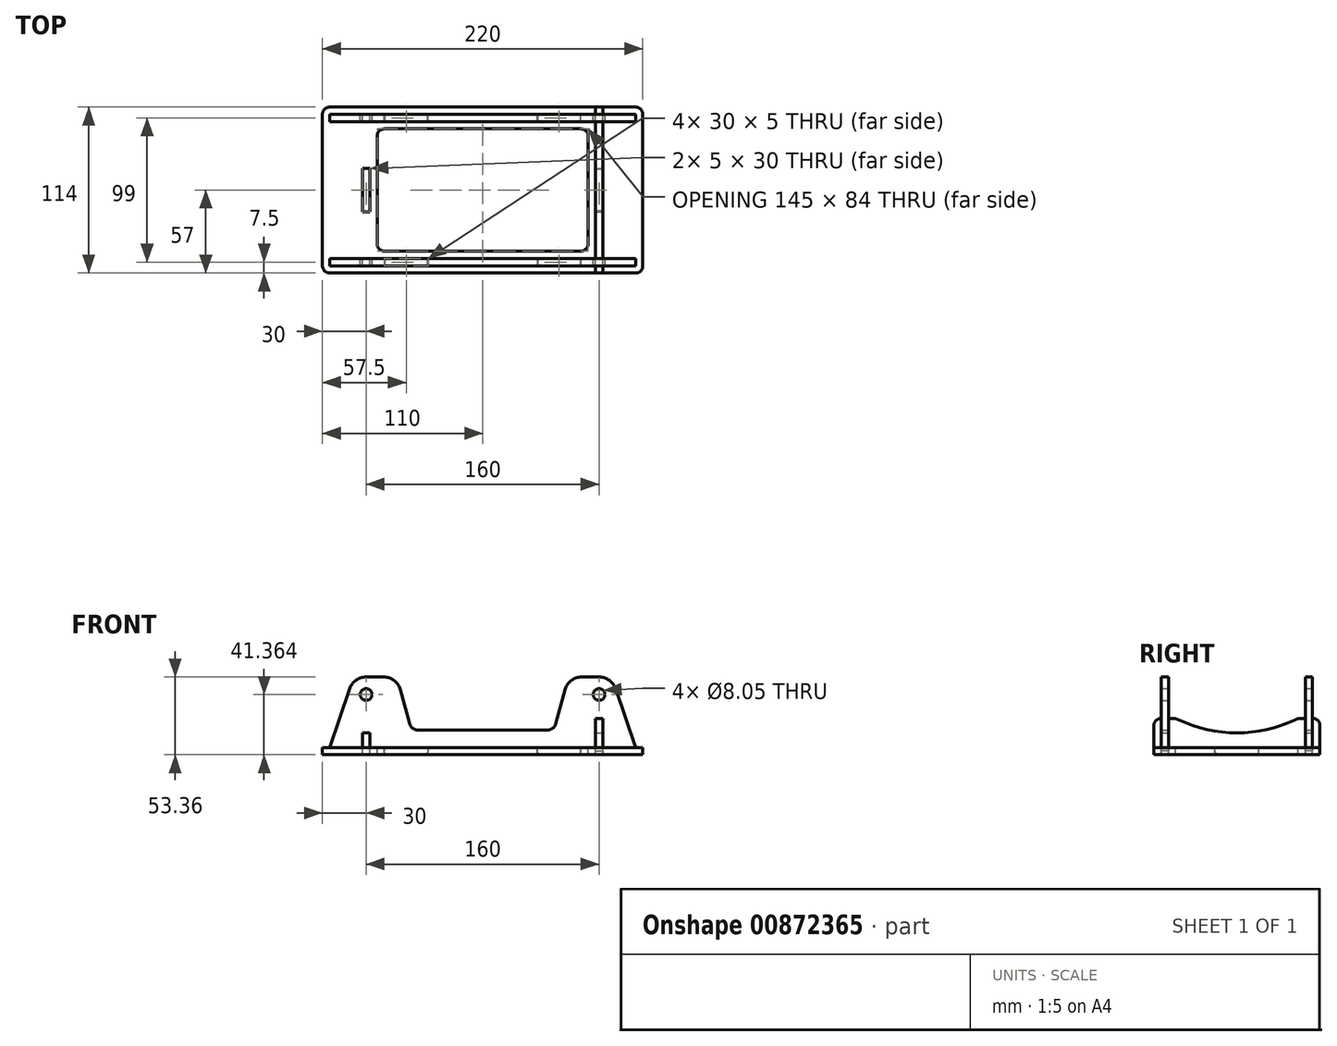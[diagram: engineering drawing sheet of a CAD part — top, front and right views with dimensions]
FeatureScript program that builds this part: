
annotation { "Feature Type Name" : "Feature", "Feature Type Description" : "" }
export const myFeature = defineFeature(function(context is Context, id is Id, definition is map)
    precondition{}
    {
        {
            var Q0;
            Q0=qCreatedBy(makeId("Front.planeOp"),FACE);
            var sketch = newSketch(context, id + "F0", { "sketchPlane" : qUnion([Q0])});
            skCircle(sketch, "E0", {"center": v(0, 135) * mm, "radius": 115 * mm, "construction": true});
            skCircle(sketch, "E1", {"center": v(0, 114.75) * mm, "radius": 100 * mm, "construction": true});
            skCircle(sketch, "E2", {"center": v(-80, 36.36) * mm, "radius": 4.03 * mm});
            skLineSegment(sketch, "E3", {"start": v(-105, 0) * mm, "end": v(-91.36, 40.22) * mm});
            skLineSegment(sketch, "E4", {"start": v(-105, 0) * mm, "end": v(-67.5, 0) * mm});
            skLineSegment(sketch, "E5", {"start": v(-80, 48.36) * mm, "end": v(-68, 48.36) * mm});
            skArc(sketch, "E6", {"start": v(-91.36, 40.22) * mm, "mid": v(-73, 26.61) * mm, "end": v(-80, 48.36) * mm, "construction": true});
            skArc(sketch, "E7", {"start": v(-80, 48.36) * mm, "mid": v(-87, 46.12) * mm, "end": v(-91.36, 40.22) * mm});
            skLineSegment(sketch, "E8.MirrorCS", {"start": v(-50.24, 16.45) * mm, "end": v(-56.4, 39.47) * mm});
            skLineSegment(sketch, "E9", {"start": v(0, 12) * mm, "end": v(-44.44, 12) * mm});
            skPoint(sketch, "E10.visualSharp", {"position": v(-49.05, 12) * mm});
            skArc(sketch, "E10.filletArc", {"start": v(-50.24, 16.45) * mm, "mid": v(-48.1, 13.24) * mm, "end": v(-44.44, 12) * mm});
            skPoint(sketch, "E11.visualSharp", {"position": v(-105, 0) * mm});
            skPoint(sketch, "E12.orphan", {"position": v(0, 0) * mm});
            skArc(sketch, "E13", {"start": v(-68, 48.36) * mm, "mid": v(-75.3, 26.84) * mm, "end": v(-56.4, 39.47) * mm, "construction": true});
            skArc(sketch, "E14", {"start": v(-56.4, 39.47) * mm, "mid": v(-60.7, 45.88) * mm, "end": v(-68, 48.36) * mm});
            skLineSegment(sketch, "E15.MirrorCS", {"start": v(105, 0) * mm, "end": v(67.5, 0) * mm});
            skLineSegment(sketch, "E16.MirrorCS", {"start": v(105, 0) * mm, "end": v(91.36, 40.22) * mm});
            skArc(sketch, "E17.MirrorCS", {"start": v(80, 48.36) * mm, "mid": v(87, 46.12) * mm, "end": v(91.36, 40.22) * mm});
            skCircle(sketch, "E18.MirrorC", {"center": v(80, 36.36) * mm, "radius": 4.03 * mm});
            skLineSegment(sketch, "E19.MirrorCS", {"start": v(80, 48.36) * mm, "end": v(68, 48.36) * mm});
            skArc(sketch, "E20.MirrorCS", {"start": v(56.4, 39.47) * mm, "mid": v(60.7, 45.88) * mm, "end": v(68, 48.36) * mm});
            skLineSegment(sketch, "E21.MirrorCS", {"start": v(50.24, 16.45) * mm, "end": v(56.4, 39.47) * mm});
            skArc(sketch, "E22.MirrorCS", {"start": v(50.24, 16.45) * mm, "mid": v(48.1, 13.24) * mm, "end": v(44.44, 12) * mm});
            skLineSegment(sketch, "E23.MirrorCS", {"start": v(0, 12) * mm, "end": v(44.44, 12) * mm});
            skLineSegment(sketch, "E24.top", {"start": v(-67.5, -5) * mm, "end": v(-37.5, -5) * mm});
            skLineSegment(sketch, "E24.left", {"start": v(-67.5, 0) * mm, "end": v(-67.5, -5) * mm});
            skLineSegment(sketch, "E24.right", {"start": v(-37.5, 0) * mm, "end": v(-37.5, -5) * mm});
            skLineSegment(sketch, "E25", {"start": v(-37.5, 0) * mm, "end": v(0, 0) * mm});
            skLineSegment(sketch, "E26.MirrorCS", {"start": v(67.5, 0) * mm, "end": v(67.5, -5) * mm});
            skLineSegment(sketch, "E27.MirrorCS", {"start": v(67.5, -5) * mm, "end": v(37.5, -5) * mm});
            skLineSegment(sketch, "E28.MirrorCS", {"start": v(37.5, 0) * mm, "end": v(37.5, -5) * mm});
            skLineSegment(sketch, "E29", {"start": v(37.5, 0) * mm, "end": v(0, 0) * mm});
            skLineSegment(sketch, "E30", {"start": v(37.5, 0) * mm, "end": v(37.5, 0) * mm});
            skLineSegment(sketch, "E31.bottom", {"start": v(-77.5, 10) * mm, "end": v(-82.5, 10) * mm});
            skLineSegment(sketch, "E31.top", {"start": v(-77.5, 0) * mm, "end": v(-82.5, 0) * mm});
            skLineSegment(sketch, "E31.left", {"start": v(-77.5, 10) * mm, "end": v(-77.5, 0) * mm});
            skLineSegment(sketch, "E31.right", {"start": v(-82.5, 10) * mm, "end": v(-82.5, 0) * mm});
            skPoint(sketch, "E31.middle", {"position": v(-80, 5) * mm});
            skLineSegment(sketch, "E32.MirrorCS", {"start": v(77.5, 10) * mm, "end": v(82.5, 10) * mm});
            skLineSegment(sketch, "E33.MirrorCS", {"start": v(82.5, 10) * mm, "end": v(82.5, 0) * mm});
            skLineSegment(sketch, "E34.MirrorCS", {"start": v(77.5, 0) * mm, "end": v(82.5, 0) * mm});
            skLineSegment(sketch, "E35.MirrorCS", {"start": v(77.5, 10) * mm, "end": v(77.5, 0) * mm});
            skSolve(sketch);
        }
        {
            var Q0;
            Q0=makeQuery(id+"F0.imprint","IMPRINT",FACE,{"disambiguationData":[TD([[makeQuery(id+"F0.imprint","IMPRINT",EDGE,{"derivedFrom":sQuery(id+"F0.wireOp",EDGE,"E2")}),-1.0]])]});
            extrude(context, id + "F1", {"entities" : qUnion([Q0]), "depth" : 5 * mm, "offsetDistance" : 25 * mm});
        }
        {
            var Q0;
            Q0=makeQuery(id+"F1.opExtrude","SWEPT_EDGE",EDGE,{"disambiguationData":[OSD([sQuery(id+"F0.wireOp",EDGE,"E24.top"),sQuery(id+"F0.wireOp",EDGE,"E24.left")])]});
            var Q1;
            Q1=makeQuery(id+"F1.opExtrude","SWEPT_EDGE",EDGE,{"disambiguationData":[OSD([sQuery(id+"F0.wireOp",EDGE,"E27.MirrorCS"),sQuery(id+"F0.wireOp",EDGE,"E28.MirrorCS")])]});
            var Q2;
            Q2=makeQuery(id+"F1.opExtrude","SWEPT_EDGE",EDGE,{"disambiguationData":[OSD([sQuery(id+"F0.wireOp",EDGE,"E24.top"),sQuery(id+"F0.wireOp",EDGE,"E24.right")])]});
            chamfer(context, id + "F2", {"entities" : qUnion([Q0, Q1, Q2]), "chamferType" : ChamferType.TWO_OFFSETS, "width1" : .5 * mm, "oppositeDirection" : false, "width2" : 2.5 * mm, "tangentPropagation" : true});
        }
        {
            var Q0;
            Q0=makeQuery(id+"F1.opExtrude","SWEPT_EDGE",EDGE,{"disambiguationData":[OSD([sQuery(id+"F0.wireOp",EDGE,"E26.MirrorCS"),sQuery(id+"F0.wireOp",EDGE,"E27.MirrorCS")])]});
            chamfer(context, id + "F3", {"entities" : qUnion([Q0]), "chamferType" : ChamferType.TWO_OFFSETS, "width1" : 2.5 * mm, "oppositeDirection" : false, "width2" : .5 * mm, "tangentPropagation" : true});
        }
        {
            var Q0;
            Q0=makeQuery(id+"F1.opExtrude","SWEPT_BODY",BODY,{"disambiguationData":[OSD([sQuery(id+"F0.wireOp",EDGE,"E2"),sQuery(id+"F0.wireOp",EDGE,"E3"),sQuery(id+"F0.wireOp",EDGE,"E4"),sQuery(id+"F0.wireOp",EDGE,"E5"),sQuery(id+"F0.wireOp",EDGE,"E7"),sQuery(id+"F0.wireOp",EDGE,"E8.MirrorCS"),sQuery(id+"F0.wireOp",EDGE,"E9"),sQuery(id+"F0.wireOp",EDGE,"E10.filletArc"),sQuery(id+"F0.wireOp",EDGE,"E14"),sQuery(id+"F0.wireOp",EDGE,"E15.MirrorCS"),sQuery(id+"F0.wireOp",EDGE,"E16.MirrorCS"),sQuery(id+"F0.wireOp",EDGE,"E17.MirrorCS"),sQuery(id+"F0.wireOp",EDGE,"E18.MirrorC"),sQuery(id+"F0.wireOp",EDGE,"E19.MirrorCS"),sQuery(id+"F0.wireOp",EDGE,"E20.MirrorCS"),sQuery(id+"F0.wireOp",EDGE,"E21.MirrorCS"),sQuery(id+"F0.wireOp",EDGE,"E22.MirrorCS"),sQuery(id+"F0.wireOp",EDGE,"E23.MirrorCS"),sQuery(id+"F0.wireOp",EDGE,"E24.top"),sQuery(id+"F0.wireOp",EDGE,"E24.left"),sQuery(id+"F0.wireOp",EDGE,"E24.right"),sQuery(id+"F0.wireOp",EDGE,"E25"),sQuery(id+"F0.wireOp",EDGE,"E26.MirrorCS"),sQuery(id+"F0.wireOp",EDGE,"E27.MirrorCS"),sQuery(id+"F0.wireOp",EDGE,"E28.MirrorCS"),sQuery(id+"F0.wireOp",EDGE,"E29"),sQuery(id+"F0.wireOp",EDGE,"E31.bottom"),sQuery(id+"F0.wireOp",EDGE,"E31.top"),sQuery(id+"F0.wireOp",EDGE,"E31.left"),sQuery(id+"F0.wireOp",EDGE,"E31.right"),sQuery(id+"F0.wireOp",EDGE,"E32.MirrorCS"),sQuery(id+"F0.wireOp",EDGE,"E33.MirrorCS"),sQuery(id+"F0.wireOp",EDGE,"E34.MirrorCS"),sQuery(id+"F0.wireOp",EDGE,"E35.MirrorCS")])]});
            transform(context, id + "F4", {"entities" : qUnion([Q0]), "transformType" : TransformType.TRANSLATION_3D, "dx" : 0 * mm, "dy" : (94 + 5) * mm, "dz" : 0 * mm, "makeCopy" : true});
        }
        {
            var Q0;
            Q0=makeQuery(id+"F4.opPattern","COPY",FACE,{"derivedFrom":makeQuery(id+"F1.opExtrude","SWEPT_FACE",FACE,{"disambiguationData":[OSD([sQuery(id+"F0.wireOp",EDGE,"E25"),sQuery(id+"F0.wireOp",EDGE,"E29")])]}),"instanceName":"1"});
            var sketch = newSketch(context, id + "F5", { "sketchPlane" : qUnion([Q0])});
            skLineSegment(sketch, "E36", {"start": v(0, 0) * mm, "end": v(0, -94) * mm, "construction": true});
            skPoint(sketch, "E37.0", {"position": v(-82.5, 0) * mm});
            skPoint(sketch, "E38.0", {"position": v(-77.5, 0) * mm});
            skPoint(sketch, "E39.0", {"position": v(-67.5, 0) * mm});
            skPoint(sketch, "E40.0", {"position": v(-37.5, 0) * mm});
            skPoint(sketch, "E41.0", {"position": v(-37.5, 5) * mm});
            skLineSegment(sketch, "E42.bottom", {"start": v(-67.5, 0) * mm, "end": v(-37.5, 0) * mm});
            skLineSegment(sketch, "E42.top", {"start": v(-67.5, 5) * mm, "end": v(-37.5, 5) * mm});
            skLineSegment(sketch, "E42.left", {"start": v(-67.5, 0) * mm, "end": v(-67.5, 5) * mm});
            skLineSegment(sketch, "E42.right", {"start": v(-37.5, 0) * mm, "end": v(-37.5, 5) * mm});
            skLineSegment(sketch, "E43", {"start": v(0, -47) * mm, "end": v(-105, -47) * mm, "construction": true});
            skPoint(sketch, "E44.0", {"position": v(-105, 0) * mm});
            skPoint(sketch, "E45.0", {"position": v(-105, -94) * mm});
            skLineSegment(sketch, "E46", {"start": v(-105, -94) * mm, "end": v(-105, 0) * mm, "construction": true});
            skLineSegment(sketch, "E47", {"start": v(0, 10) * mm, "end": v(-105, 10) * mm});
            skLineSegment(sketch, "E48", {"start": v(-110, 5) * mm, "end": v(-110, -47) * mm});
            skPoint(sketch, "E49.visualSharp", {"position": v(-110, 10) * mm});
            skArc(sketch, "E49.filletArc", {"start": v(-105, 10) * mm, "mid": v(-108.54, 8.54) * mm, "end": v(-110, 5) * mm});
            skLineSegment(sketch, "E50", {"start": v(-72.5, -47) * mm, "end": v(-72.5, -10) * mm});
            skLineSegment(sketch, "E51", {"start": v(-67.5, -5) * mm, "end": v(0, -5) * mm});
            skPoint(sketch, "E52.visualSharp", {"position": v(-72.5, -5) * mm});
            skArc(sketch, "E52.filletArc", {"start": v(-67.5, -5) * mm, "mid": v(-71.04, -6.46) * mm, "end": v(-72.5, -10) * mm});
            skLineSegment(sketch, "E53", {"start": v(-77.5, -47) * mm, "end": v(-77.5, -32) * mm});
            skLineSegment(sketch, "E54", {"start": v(-77.5, -32) * mm, "end": v(-82.5, -32) * mm});
            skLineSegment(sketch, "E55", {"start": v(-82.5, -32) * mm, "end": v(-82.5, -47) * mm});
            skLineSegment(sketch, "E56.MirrorCS", {"start": v(-110, -99) * mm, "end": v(-110, -47) * mm});
            skArc(sketch, "E57.MirrorCS", {"start": v(-105, -104) * mm, "mid": v(-108.54, -102.54) * mm, "end": v(-110, -99) * mm});
            skLineSegment(sketch, "E58.MirrorCS", {"start": v(0, -104) * mm, "end": v(-105, -104) * mm});
            skLineSegment(sketch, "E59.MirrorCS", {"start": v(-67.5, -89) * mm, "end": v(0, -89) * mm});
            skArc(sketch, "E60.MirrorCS", {"start": v(-67.5, -89) * mm, "mid": v(-71.04, -87.54) * mm, "end": v(-72.5, -84) * mm});
            skLineSegment(sketch, "E61.MirrorCS", {"start": v(-72.5, -47) * mm, "end": v(-72.5, -84) * mm});
            skLineSegment(sketch, "E62.MirrorCS", {"start": v(-82.5, -62) * mm, "end": v(-82.5, -47) * mm});
            skLineSegment(sketch, "E63.MirrorCS", {"start": v(-77.5, -62) * mm, "end": v(-82.5, -62) * mm});
            skLineSegment(sketch, "E64.MirrorCS", {"start": v(-77.5, -47) * mm, "end": v(-77.5, -62) * mm});
            skLineSegment(sketch, "E65.MirrorCS", {"start": v(0, 10) * mm, "end": v(105, 10) * mm});
            skLineSegment(sketch, "E66.MirrorCS", {"start": v(67.5, -5) * mm, "end": v(0, -5) * mm});
            skArc(sketch, "E67.MirrorCS", {"start": v(67.5, -5) * mm, "mid": v(71.04, -6.46) * mm, "end": v(72.5, -10) * mm});
            skLineSegment(sketch, "E68.MirrorCS", {"start": v(72.5, -47) * mm, "end": v(72.5, -10) * mm});
            skLineSegment(sketch, "E69.MirrorCS", {"start": v(72.5, -47) * mm, "end": v(72.5, -84) * mm});
            skArc(sketch, "E70.MirrorCS", {"start": v(67.5, -89) * mm, "mid": v(71.04, -87.54) * mm, "end": v(72.5, -84) * mm});
            skLineSegment(sketch, "E71.MirrorCS", {"start": v(67.5, -89) * mm, "end": v(0, -89) * mm});
            skArc(sketch, "E72.MirrorCS", {"start": v(105, 10) * mm, "mid": v(108.54, 8.54) * mm, "end": v(110, 5) * mm});
            skLineSegment(sketch, "E73.MirrorCS", {"start": v(110, 5) * mm, "end": v(110, -47) * mm});
            skArc(sketch, "E74.MirrorCS", {"start": v(105, -104) * mm, "mid": v(108.54, -102.54) * mm, "end": v(110, -99) * mm});
            skLineSegment(sketch, "E75.MirrorCS", {"start": v(0, -104) * mm, "end": v(105, -104) * mm});
            skLineSegment(sketch, "E76.MirrorCS", {"start": v(110, -99) * mm, "end": v(110, -47) * mm});
            skLineSegment(sketch, "E77.MirrorCS", {"start": v(77.5, -47) * mm, "end": v(77.5, -62) * mm});
            skLineSegment(sketch, "E78.MirrorCS", {"start": v(77.5, -62) * mm, "end": v(82.5, -62) * mm});
            skLineSegment(sketch, "E79.MirrorCS", {"start": v(82.5, -62) * mm, "end": v(82.5, -47) * mm});
            skLineSegment(sketch, "E80.MirrorCS", {"start": v(82.5, -32) * mm, "end": v(82.5, -47) * mm});
            skLineSegment(sketch, "E81.MirrorCS", {"start": v(77.5, -32) * mm, "end": v(82.5, -32) * mm});
            skLineSegment(sketch, "E82.MirrorCS", {"start": v(77.5, -47) * mm, "end": v(77.5, -32) * mm});
            skLineSegment(sketch, "E83.MirrorCS", {"start": v(67.5, 0) * mm, "end": v(37.5, 0) * mm});
            skLineSegment(sketch, "E84.MirrorCS", {"start": v(37.5, 0) * mm, "end": v(37.5, 5) * mm});
            skLineSegment(sketch, "E85.MirrorCS", {"start": v(67.5, 5) * mm, "end": v(37.5, 5) * mm});
            skLineSegment(sketch, "E86.MirrorCS", {"start": v(67.5, 0) * mm, "end": v(67.5, 5) * mm});
            skLineSegment(sketch, "E87.MirrorCS", {"start": v(67.5, -99) * mm, "end": v(37.5, -99) * mm});
            skLineSegment(sketch, "E88.MirrorCS", {"start": v(67.5, -94) * mm, "end": v(67.5, -99) * mm});
            skLineSegment(sketch, "E89.MirrorCS", {"start": v(37.5, -94) * mm, "end": v(37.5, -99) * mm});
            skLineSegment(sketch, "E90.MirrorCS", {"start": v(67.5, -94) * mm, "end": v(37.5, -94) * mm});
            skLineSegment(sketch, "E91.MirrorCS", {"start": v(-37.5, -94) * mm, "end": v(-37.5, -99) * mm});
            skPoint(sketch, "E92.MirrorP", {"position": v(-37.5, -94) * mm});
            skLineSegment(sketch, "E93.MirrorCS", {"start": v(-67.5, -99) * mm, "end": v(-37.5, -99) * mm});
            skPoint(sketch, "E94.MirrorP", {"position": v(-67.5, -94) * mm});
            skLineSegment(sketch, "E95.MirrorCS", {"start": v(-67.5, -94) * mm, "end": v(-67.5, -99) * mm});
            skLineSegment(sketch, "E96.MirrorCS", {"start": v(-67.5, -94) * mm, "end": v(-37.5, -94) * mm});
            skPoint(sketch, "E97.MirrorP", {"position": v(-37.5, -99) * mm});
            skSolve(sketch);
        }
        {
            var Q0;
            Q0 = qSketchRegion(id + "F5", true);
            extrude(context, id + "F6", {"entities" : qUnion([Q0]), "depth" : 5 * mm, "offsetDistance" : 25 * mm});
        }
        {
            var Q0;
            Q0=makeQuery(id+"F1.opExtrude","SWEPT_FACE",FACE,{"disambiguationData":[OSD([sQuery(id+"F0.wireOp",EDGE,"E35.MirrorCS")])]});
            var sketch = newSketch(context, id + "F7", { "sketchPlane" : qUnion([Q0])});
            skLineSegment(sketch, "E98.0", {"start": v(-5, 10) * mm, "end": v(-5, 20) * mm});
            skLineSegment(sketch, "E99.0", {"start": v(0, 10) * mm, "end": v(0, 20) * mm});
            skLineSegment(sketch, "E100.0", {"start": v(32, -5) * mm, "end": v(62, -5) * mm});
            skLineSegment(sketch, "E101.0", {"start": v(32, -5) * mm, "end": v(32, 0) * mm});
            skLineSegment(sketch, "E102.0", {"start": v(62, -5) * mm, "end": v(62, 0) * mm});
            skPoint(sketch, "E103.0", {"position": v(-10, 0) * mm});
            skLineSegment(sketch, "E104", {"start": v(-10, 20) * mm, "end": v(-5, 20) * mm});
            skLineSegment(sketch, "E105", {"start": v(-10, 0) * mm, "end": v(-10, 20) * mm});
            skPoint(sketch, "E106.orphan", {"position": v(-5, 40.22) * mm});
            skPoint(sketch, "E107", {"position": v(-5, 10) * mm});
            skPoint(sketch, "E108.start.orphan", {"position": v(-5, 0) * mm});
            skLineSegment(sketch, "E109", {"start": v(-10, 0) * mm, "end": v(32, 0) * mm});
            skPoint(sketch, "E110.0", {"position": v(0, 10) * mm});
            skLineSegment(sketch, "E111", {"start": v(-5, 10) * mm, "end": v(0, 10) * mm});
            skPoint(sketch, "E112", {"position": v(0, 20) * mm});
            skPoint(sketch, "E113.orphan", {"position": v(0, 40.22) * mm});
            skPoint(sketch, "E114.orphan", {"position": v(0, 0) * mm});
            skLineSegment(sketch, "E115", {"start": v(0, 20) * mm, "end": v(5, 20) * mm});
            skArc(sketch, "E116", {"start": v(5, 20) * mm, "mid": v(25.41, 12.53) * mm, "end": v(47, 10) * mm});
            skPoint(sketch, "E116.endSnap0", {"position": v(47, -5) * mm});
            skLineSegment(sketch, "E117", {"start": v(0, 10) * mm, "end": v(47, 10) * mm, "construction": true});
            skLineSegment(sketch, "E118", {"start": v(47, 10) * mm, "end": v(47, -5) * mm, "construction": true});
            skArc(sketch, "E119.MirrorCS", {"start": v(89, 20) * mm, "mid": v(68.59, 12.53) * mm, "end": v(47, 10) * mm});
            skLineSegment(sketch, "E120.MirrorCS", {"start": v(94, 20) * mm, "end": v(89, 20) * mm});
            skLineSegment(sketch, "E121.MirrorCS", {"start": v(94, 10) * mm, "end": v(94, 20) * mm});
            skLineSegment(sketch, "E122.MirrorCS", {"start": v(99, 10) * mm, "end": v(94, 10) * mm});
            skLineSegment(sketch, "E123.MirrorCS", {"start": v(99, 10) * mm, "end": v(99, 20) * mm});
            skLineSegment(sketch, "E124.MirrorCS", {"start": v(104, 20) * mm, "end": v(99, 20) * mm});
            skLineSegment(sketch, "E125.MirrorCS", {"start": v(104, 0) * mm, "end": v(104, 20) * mm});
            skLineSegment(sketch, "E126.MirrorCS", {"start": v(104, 0) * mm, "end": v(62, 0) * mm});
            skSolve(sketch);
        }
        {
            var Q0;
            Q0 = qSketchRegion(id + "F7", true);
            extrude(context, id + "F8", {"entities" : qUnion([Q0]), "depth" : 5 * mm, "offsetDistance" : 25 * mm});
        }
        {
            var Q0;
            Q0=makeQuery(id+"F8.opExtrude","SWEPT_EDGE",EDGE,{"disambiguationData":[OSD([sQuery(id+"F7.wireOp",EDGE,"E104"),sQuery(id+"F7.wireOp",EDGE,"E105")])]});
            var Q1;
            Q1=makeQuery(id+"F8.opExtrude","SWEPT_EDGE",EDGE,{"disambiguationData":[OSD([sQuery(id+"F7.wireOp",EDGE,"E124.MirrorCS"),sQuery(id+"F7.wireOp",EDGE,"E125.MirrorCS")])]});
            fillet(context, id + "F9", {"entities" : qUnion([Q0, Q1]), "radius" : 5 * mm, "tangentPropagation" : true, "allowEdgeOverflow" : false});
        }
        {
            var Q0;
            Q0=makeQuery(id+"F8.opExtrude","SWEPT_EDGE",EDGE,{"disambiguationData":[OSD([sQuery(id+"F7.wireOp",EDGE,"E115"),sQuery(id+"F7.wireOp",EDGE,"E116")])]});
            var Q1;
            Q1=makeQuery(id+"F8.opExtrude","SWEPT_EDGE",EDGE,{"disambiguationData":[OSD([sQuery(id+"F7.wireOp",EDGE,"E119.MirrorCS"),sQuery(id+"F7.wireOp",EDGE,"E120.MirrorCS")])]});
            fillet(context, id + "F10", {"entities" : qUnion([Q0, Q1]), "radius" : 10 * mm, "tangentPropagation" : true, "allowEdgeOverflow" : false});
        }
        {
            var Q0;
            Q0=makeQuery(id+"F8.opExtrude","SWEPT_EDGE",EDGE,{"disambiguationData":[OSD([sQuery(id+"F7.wireOp",EDGE,"E100.0"),sQuery(id+"F7.wireOp",EDGE,"E101.0")])]});
            var Q1;
            Q1=makeQuery(id+"F8.opExtrude","SWEPT_EDGE",EDGE,{"disambiguationData":[OSD([sQuery(id+"F7.wireOp",EDGE,"E100.0"),sQuery(id+"F7.wireOp",EDGE,"E102.0")])]});
            chamfer(context, id + "F11", {"entities" : qUnion([Q0, Q1]), "chamferType" : ChamferType.TWO_OFFSETS, "width1" : .5 * mm, "oppositeDirection" : false, "width2" : 2.5 * mm, "tangentPropagation" : true});
        }
    });
